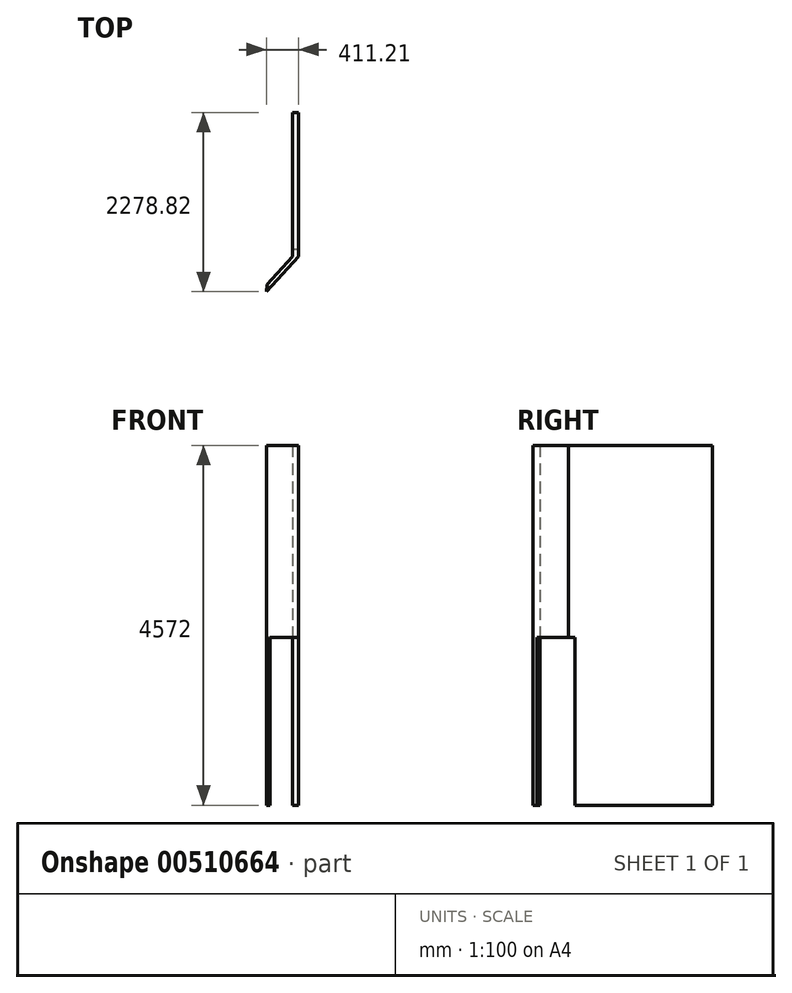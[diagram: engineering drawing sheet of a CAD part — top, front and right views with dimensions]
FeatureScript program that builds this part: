
annotation { "Feature Type Name" : "Feature", "Feature Type Description" : "" }
export const myFeature = defineFeature(function(context is Context, id is Id, definition is map)
    precondition{}
    {
        {
            var Q0;
            Q0=qCreatedBy(makeId("Top.planeOp"),FACE);
            var sketch = newSketch(context, id + "F0", { "sketchPlane" : qUnion([Q0])});
            skLineSegment(sketch, "E0", {"start": v(255.75, 2471.91) * mm, "end": v(255.75, 643.11) * mm});
            skLineSegment(sketch, "E1", {"start": v(255.75, 643.11) * mm, "end": v(-155.46, 193.1) * mm});
            skLineSegment(sketch, "E2", {"start": v(-149.42, 283.1) * mm, "end": v(179.55, 643.11) * mm});
            skLineSegment(sketch, "E3", {"start": v(179.55, 643.11) * mm, "end": v(179.55, 2471.91) * mm});
            skLineSegment(sketch, "E4", {"start": v(179.55, 2471.91) * mm, "end": v(255.75, 2471.91) * mm});
            skLineSegment(sketch, "E5", {"start": v(-149.42, 283.1) * mm, "end": v(-155.46, 193.1) * mm});
            skSolve(sketch);
        }
        {
            var Q0;
            Q0 = qSketchRegion(id + "F0", true);
            extrude(context, id + "F1", {"entities" : qUnion([Q0]), "depth" : 4572 * mm, "offsetDistance" : 30.48 * mm});
        }
        {
            var Q0;
            Q0=makeQuery(id+"F1.opExtrude","SWEPT_FACE",FACE,{"disambiguationData":[OSD([sQuery(id+"F0.wireOp",EDGE,"E2")])]});
            var sketch = newSketch(context, id + "F2", { "sketchPlane" : qUnion([Q0])});
            skLineSegment(sketch, "E6.bottom", {"start": v(-595.87, 2133.6) * mm, "end": v(-108.2, 2133.6) * mm});
            skLineSegment(sketch, "E6.top", {"start": v(-595.87, 0) * mm, "end": v(-108.2, 0) * mm});
            skLineSegment(sketch, "E6.left", {"start": v(-595.87, 2133.6) * mm, "end": v(-595.87, 0) * mm});
            skLineSegment(sketch, "E6.right", {"start": v(-108.2, 2133.6) * mm, "end": v(-108.2, 0) * mm});
            skSolve(sketch);
        }
        {
            var Q0;
            Q0 = qSketchRegion(id + "F2", true);
            extrude(context, id + "F3", {"entities" : qUnion([Q0]), "operationType" : NewBodyOperationType.REMOVE, "oppositeDirection" : true, "depth" : 76.2 * mm, "offsetDistance" : 30.48 * mm});
        }
        {
            var Q0;
            Q0=makeQuery(id+"F1.opExtrude","SWEPT_FACE",FACE,{"disambiguationData":[OSD([sQuery(id+"F0.wireOp",EDGE,"E3")])]});
            var sketch = newSketch(context, id + "F4", { "sketchPlane" : qUnion([Q0])});
            skLineSegment(sketch, "E7.bottom", {"start": v(-727.08, 2133.6) * mm, "end": v(-605.16, 2133.6) * mm});
            skLineSegment(sketch, "E7.top", {"start": v(-727.08, 0) * mm, "end": v(-605.16, 0) * mm});
            skLineSegment(sketch, "E7.left", {"start": v(-727.08, 2133.6) * mm, "end": v(-727.08, 0) * mm});
            skLineSegment(sketch, "E7.right", {"start": v(-605.16, 2133.6) * mm, "end": v(-605.16, 0) * mm});
            skSolve(sketch);
        }
        {
            var Q0;
            Q0 = qSketchRegion(id + "F4", true);
            extrude(context, id + "F5", {"entities" : qUnion([Q0]), "operationType" : NewBodyOperationType.REMOVE, "oppositeDirection" : true, "depth" : 76.2 * mm, "offsetDistance" : 30.48 * mm});
        }
    });
